# Revit family: 4318_Conventional Heat Detector
name_source: partatom
category: Fire Alarm Devices
units: mm (PartAtom-declared; Revit-internal decimal feet)

## family parameters
Cut with Voids When Loaded = No
Host = Face
Maintain Annotation Orientation = No
OmniClass Number = 23.85.30.21
OmniClass Title = Environmental Detection/Registration
Part Type = Normal
Room Calculation Point = No
Round Connector Dimension = Use Diameter
Shared = No

## types (2) — shared parameters
Ambient Humidity = Maximum 95 % RH
Ambient Temperature Operating = -10 to +50 °C
Ambient Temperature Storage = -25 to +70 °C
CPR = 0786-CPR-21198
Clearance Area = Clearance Area
Current (Active) = Min. 3 mA
Current Quiescent = 0.015 mA
H_Base (mm) = 13 mm
H_Detector (mm) = 39 mm  [stored 0.127953 ft]
H_Total (mm) = 52 mm
Ingress Protection Rating = IP51
Manufacturer = Panasonic
Max_Wire Size = Ø 1.6 mm (2 mm²)
Min_Wire Size = Ø 0.65 mm (0.3 mm²)
Omniclass Code = 23.85.30.21.11.11.11
Omniclass Description = Smoke Detectors
Tested and Approved = EN54-5
URL = https://www.panasonic-fire-security.com
Uniclass 2015 Code = Pr_75_80_30_27
Uniclass 2015 Description = Fire and smoke detector bases
Uniformat 2010  Code = D7050
Uniformat 2010 Description = Detection and Alarm
Vds Approval = G208048
Version = RVT20
Voltage Allowed = 12 – 30 VDC
Voltage Normal = 24 VDC
Weight = 54g
ø (mm) = 102 mm
zero-valued in all types: Default Elevation

## per-type parameters (varying)
| type | Bases | Description | Model | Product Material | Type Comments |
| 4318_2423 | Base_2324 : 2423 | Conventional heat detector 4318 with 2423 conventional base | 4318 | Polycarbonate_Panasonic_Grey | The combination heat detector 4318 is a conventional fixed temperature detector, category A1R. The detector will give an alarm at a certain fixed temperature (59 °C) and/or at a certain temperature rise, "rate-of-rise" function. |
| 4318W_2423W | Base_2324 : 2423W | Conventional heat detector 4318W with 2423W conventional base | 4318W | Polycarbonate_Panasonic_White | The combination heat detector 4318W is a conventional fixed temperature detector, category A1R. The detector will give an alarm at a certain fixed temperature (59 °C) and/or at a certain temperature rise, "rate-of-rise" function. |

note: [stored X ft] marks values corroborated as IEEE doubles in the binary element streams (Revit-internal decimal feet)

## geometry (parser evidence)
native form markers: Blend x88, Sweep x3
no freeform markers — native parametric forms only
